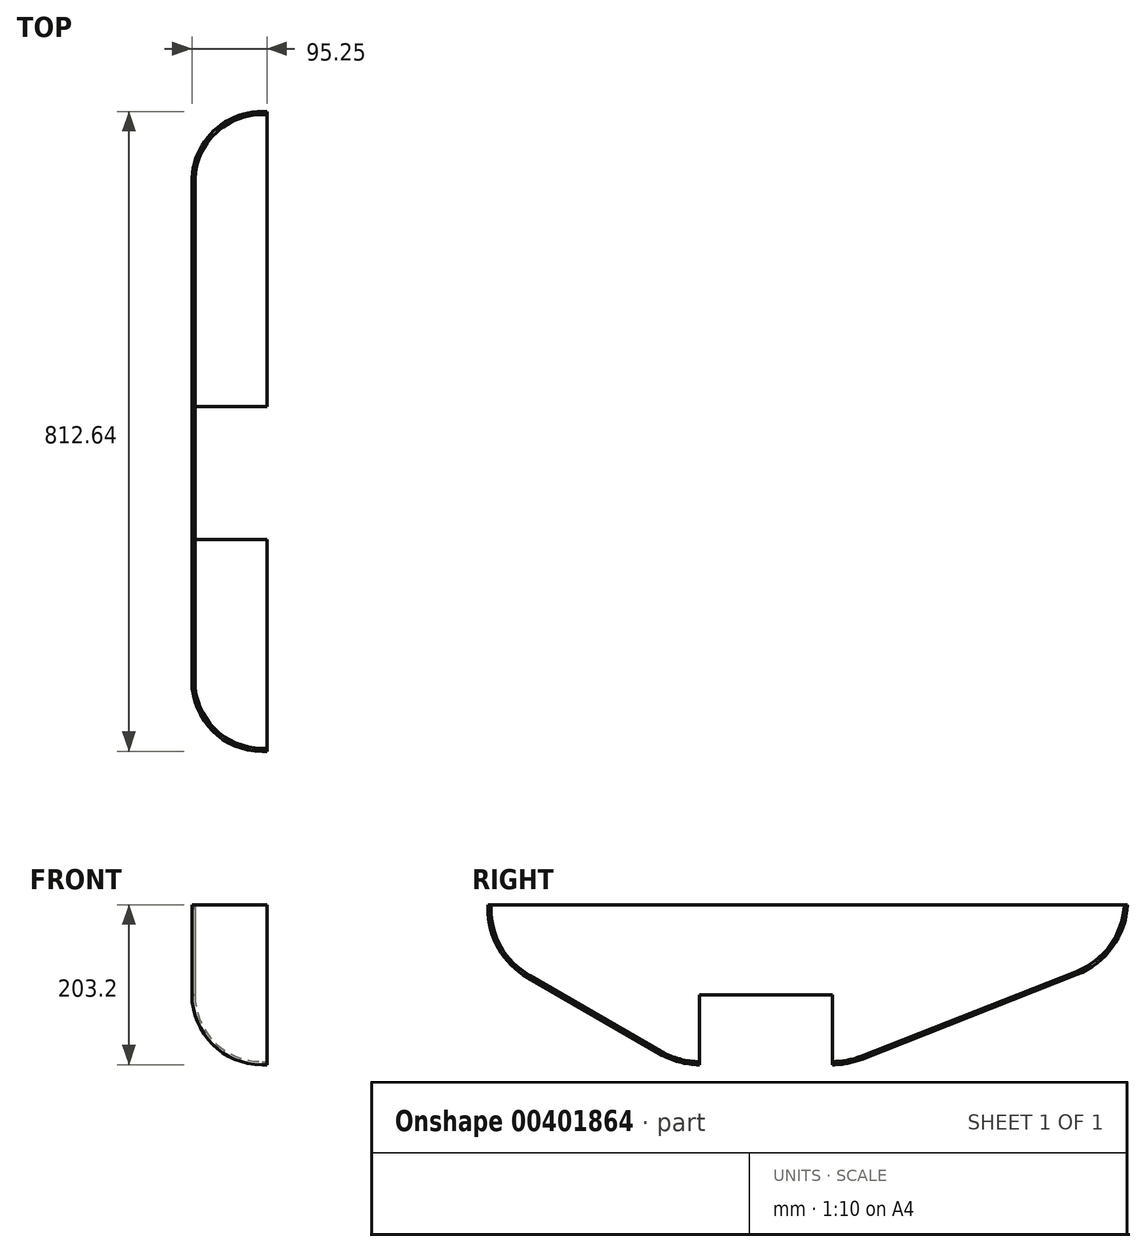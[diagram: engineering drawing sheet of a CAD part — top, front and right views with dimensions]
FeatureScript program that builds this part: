
annotation { "Feature Type Name" : "Feature", "Feature Type Description" : "" }
export const myFeature = defineFeature(function(context is Context, id is Id, definition is map)
    precondition{}
    {
        {
            var Q0;
            Q0=qCreatedBy(makeId("Top.planeOp"),FACE);
            var sketch = newSketch(context, id + "F0", { "sketchPlane" : qUnion([Q0])});
            skLineSegment(sketch, "E0.bottom", {"start": v(95.25, 406.4) * mm, "end": v(-95.25, 406.4) * mm});
            skLineSegment(sketch, "E0.top", {"start": v(95.25, -406.4) * mm, "end": v(-95.25, -406.4) * mm});
            skLineSegment(sketch, "E0.left", {"start": v(95.25, 406.4) * mm, "end": v(95.25, -406.4) * mm});
            skLineSegment(sketch, "E0.right", {"start": v(-95.25, 406.4) * mm, "end": v(-95.25, -406.4) * mm});
            skPoint(sketch, "E0.middle", {"position": v(0, 0) * mm});
            skSolve(sketch);
        }
        {
            var Q0;
            Q0=qSketchRegion(id+"F0",true);
            extrude(context, id + "F1", {"entities" : qUnion([Q0]), "depth" : 406.4 * mm});
        }
        {
            var Q0;
            Q0=makeQuery(id+"F1.opExtrude","CAP_EDGE",EDGE,{"disambiguationData":[OSD([sQuery(id+"F0.wireOp",EDGE,"E0.top")])],"isStart":false});
            var Q1;
            Q1=makeQuery(id+"F1.opExtrude","CAP_EDGE",EDGE,{"disambiguationData":[OSD([sQuery(id+"F0.wireOp",EDGE,"E0.top")])],"isStart":true});
            chamfer(context, id + "F2", {"entities" : qUnion([Q0, Q1]), "chamferType" : ChamferType.OFFSET_ANGLE, "width" : 139.7 * mm, "oppositeDirection" : false, "angle" : 60 * degree, "tangentPropagation" : true});
        }
        {
            var Q0;
            Q0=makeQuery(id+"F1.opExtrude","CAP_EDGE",EDGE,{"disambiguationData":[OSD([sQuery(id+"F0.wireOp",EDGE,"E0.bottom")])],"isStart":false});
            var Q1;
            Q1=makeQuery(id+"F1.opExtrude","CAP_EDGE",EDGE,{"disambiguationData":[OSD([sQuery(id+"F0.wireOp",EDGE,"E0.bottom")])],"isStart":true});
            chamfer(context, id + "F3", {"entities" : qUnion([Q0, Q1]), "chamferType" : ChamferType.TWO_OFFSETS, "width1" : 355.6 * mm, "oppositeDirection" : false, "width2" : 139.7 * mm, "tangentPropagation" : true});
        }
        {
            var Q0;
            {var subQ0=sQuery(id+"F0.wireOp",EDGE,"E0.top");Q0=makeQuery(id+"F2.opChamfer","BLEND_EDGE",EDGE,{"blendedFrom":[makeQuery(id+"F1.opExtrude","CAP_EDGE",EDGE,{"disambiguationData":[OSD([subQ0])],"isStart":false}),makeQuery(id+"F1.opExtrude","SWEPT_FACE",FACE,{"disambiguationData":[OSD([subQ0])]})],"blendedInto":[makeQuery(id+"F1.opExtrude","SWEPT_FACE",FACE,{"disambiguationData":[OSD([subQ0])]})]});}
            var Q1;
            {var subQ0=sQuery(id+"F0.wireOp",EDGE,"E0.top");Q1=makeQuery(id+"F2.opChamfer","BLEND_EDGE",EDGE,{"blendedFrom":[makeQuery(id+"F1.opExtrude","CAP_EDGE",EDGE,{"disambiguationData":[OSD([subQ0])],"isStart":false}),makeQuery(id+"F1.opExtrude","CAP_FACE",FACE,{"disambiguationData":[OSD([sQuery(id+"F0.wireOp",EDGE,"E0.bottom"),subQ0,sQuery(id+"F0.wireOp",EDGE,"E0.left"),sQuery(id+"F0.wireOp",EDGE,"E0.right")])],"isStart":false})],"blendedInto":[makeQuery(id+"F1.opExtrude","CAP_FACE",FACE,{"disambiguationData":[OSD([sQuery(id+"F0.wireOp",EDGE,"E0.bottom"),subQ0,sQuery(id+"F0.wireOp",EDGE,"E0.left"),sQuery(id+"F0.wireOp",EDGE,"E0.right")])],"isStart":false})]});}
            var Q2;
            {var subQ0=sQuery(id+"F0.wireOp",EDGE,"E0.bottom");Q2=makeQuery(id+"F3.opChamfer","BLEND_EDGE",EDGE,{"blendedFrom":[makeQuery(id+"F1.opExtrude","CAP_EDGE",EDGE,{"disambiguationData":[OSD([subQ0])],"isStart":false}),makeQuery(id+"F1.opExtrude","CAP_FACE",FACE,{"disambiguationData":[OSD([subQ0,sQuery(id+"F0.wireOp",EDGE,"E0.top"),sQuery(id+"F0.wireOp",EDGE,"E0.left"),sQuery(id+"F0.wireOp",EDGE,"E0.right")])],"isStart":false})],"blendedInto":[makeQuery(id+"F1.opExtrude","CAP_FACE",FACE,{"disambiguationData":[OSD([subQ0,sQuery(id+"F0.wireOp",EDGE,"E0.top"),sQuery(id+"F0.wireOp",EDGE,"E0.left"),sQuery(id+"F0.wireOp",EDGE,"E0.right")])],"isStart":false})]});}
            var Q3;
            {var subQ0=sQuery(id+"F0.wireOp",EDGE,"E0.bottom");Q3=makeQuery(id+"F3.opChamfer","BLEND_EDGE",EDGE,{"blendedFrom":[makeQuery(id+"F1.opExtrude","CAP_EDGE",EDGE,{"disambiguationData":[OSD([subQ0])],"isStart":false}),makeQuery(id+"F1.opExtrude","SWEPT_FACE",FACE,{"disambiguationData":[OSD([subQ0])]})],"blendedInto":[makeQuery(id+"F1.opExtrude","SWEPT_FACE",FACE,{"disambiguationData":[OSD([subQ0])]})]});}
            var Q4;
            {var subQ0=sQuery(id+"F0.wireOp",EDGE,"E0.bottom");Q4=makeQuery(id+"F3.opChamfer","BLEND_EDGE",EDGE,{"blendedFrom":[makeQuery(id+"F1.opExtrude","CAP_EDGE",EDGE,{"disambiguationData":[OSD([subQ0])],"isStart":true}),makeQuery(id+"F1.opExtrude","SWEPT_FACE",FACE,{"disambiguationData":[OSD([subQ0])]})],"blendedInto":[makeQuery(id+"F1.opExtrude","SWEPT_FACE",FACE,{"disambiguationData":[OSD([subQ0])]})]});}
            var Q5;
            {var subQ0=sQuery(id+"F0.wireOp",EDGE,"E0.bottom");Q5=makeQuery(id+"F3.opChamfer","BLEND_EDGE",EDGE,{"blendedFrom":[makeQuery(id+"F1.opExtrude","CAP_EDGE",EDGE,{"disambiguationData":[OSD([subQ0])],"isStart":true}),makeQuery(id+"F1.opExtrude","CAP_FACE",FACE,{"disambiguationData":[OSD([subQ0,sQuery(id+"F0.wireOp",EDGE,"E0.top"),sQuery(id+"F0.wireOp",EDGE,"E0.left"),sQuery(id+"F0.wireOp",EDGE,"E0.right")])],"isStart":true})],"blendedInto":[makeQuery(id+"F1.opExtrude","CAP_FACE",FACE,{"disambiguationData":[OSD([subQ0,sQuery(id+"F0.wireOp",EDGE,"E0.top"),sQuery(id+"F0.wireOp",EDGE,"E0.left"),sQuery(id+"F0.wireOp",EDGE,"E0.right")])],"isStart":true})]});}
            var Q6;
            {var subQ0=sQuery(id+"F0.wireOp",EDGE,"E0.top");Q6=makeQuery(id+"F2.opChamfer","BLEND_EDGE",EDGE,{"blendedFrom":[makeQuery(id+"F1.opExtrude","CAP_EDGE",EDGE,{"disambiguationData":[OSD([subQ0])],"isStart":true}),makeQuery(id+"F1.opExtrude","CAP_FACE",FACE,{"disambiguationData":[OSD([sQuery(id+"F0.wireOp",EDGE,"E0.bottom"),subQ0,sQuery(id+"F0.wireOp",EDGE,"E0.left"),sQuery(id+"F0.wireOp",EDGE,"E0.right")])],"isStart":true})],"blendedInto":[makeQuery(id+"F1.opExtrude","CAP_FACE",FACE,{"disambiguationData":[OSD([sQuery(id+"F0.wireOp",EDGE,"E0.bottom"),subQ0,sQuery(id+"F0.wireOp",EDGE,"E0.left"),sQuery(id+"F0.wireOp",EDGE,"E0.right")])],"isStart":true})]});}
            var Q7;
            {var subQ0=sQuery(id+"F0.wireOp",EDGE,"E0.top");Q7=makeQuery(id+"F2.opChamfer","BLEND_EDGE",EDGE,{"blendedFrom":[makeQuery(id+"F1.opExtrude","CAP_EDGE",EDGE,{"disambiguationData":[OSD([subQ0])],"isStart":true}),makeQuery(id+"F1.opExtrude","SWEPT_FACE",FACE,{"disambiguationData":[OSD([subQ0])]})],"blendedInto":[makeQuery(id+"F1.opExtrude","SWEPT_FACE",FACE,{"disambiguationData":[OSD([subQ0])]})]});}
            fillet(context, id + "F4", {"entities" : qUnion([Q0, Q1, Q2, Q3, Q4, Q5, Q6, Q7]), "radius" : 101.6 * mm, "tangentPropagation" : true, "allowEdgeOverflow" : false});
        }
        {
            var Q0;
            Q0=makeQuery(id+"F1.opExtrude","SWEPT_FACE",FACE,{"disambiguationData":[OSD([sQuery(id+"F0.wireOp",EDGE,"E0.left")])]});
            var Q1;
            Q1=makeQuery(id+"F1.opExtrude","SWEPT_FACE",FACE,{"disambiguationData":[OSD([sQuery(id+"F0.wireOp",EDGE,"E0.right")])]});
            fillet(context, id + "F5", {"entities" : qUnion([Q0, Q1]), "radius" : 88.9 * mm, "tangentPropagation" : true, "allowEdgeOverflow" : false});
        }
        {
            var Q0;
            {var subQ0=sQuery(id+"F0.wireOp",EDGE,"E0.left");Q0=makeQuery(id+"F5.opFillet","BLEND_FACE",FACE,{"disambiguationData":[OSD([subQ0]),TDD([makeQuery(id+"F1.opExtrude","CAP_EDGE",EDGE,{"disambiguationData":[OSD([subQ0])],"isStart":true})])]});}
            var Q1;
            Q1=makeQuery(id+"F1.opExtrude","CAP_FACE",FACE,{"disambiguationData":[OSD([sQuery(id+"F0.wireOp",EDGE,"E0.bottom"),sQuery(id+"F0.wireOp",EDGE,"E0.top"),sQuery(id+"F0.wireOp",EDGE,"E0.left"),sQuery(id+"F0.wireOp",EDGE,"E0.right")])],"isStart":true});
            var Q2;
            {var subQ0=sQuery(id+"F0.wireOp",EDGE,"E0.right");Q2=makeQuery(id+"F5.opFillet","BLEND_FACE",FACE,{"disambiguationData":[OSD([subQ0]),TDD([makeQuery(id+"F1.opExtrude","CAP_EDGE",EDGE,{"disambiguationData":[OSD([subQ0])],"isStart":true})])]});}
            shell(context, id + "F6", {"entities" : qUnion([Q0, Q1, Q2]), "thickness" : 3.8 * mm});
        }
        {
            var Q0;
            Q0=makeQuery(id+"F1.opExtrude","SWEPT_FACE",FACE,{"disambiguationData":[OSD([sQuery(id+"F0.wireOp",EDGE,"E0.left")])]});
            var sketch = newSketch(context, id + "F7", { "sketchPlane" : qUnion([Q0])});
            skLineSegment(sketch, "E1.bottom", {"start": v(-468.9, 458.17) * mm, "end": v(569.73, 458.17) * mm});
            skLineSegment(sketch, "E1.top", {"start": v(-468.9, 203.2) * mm, "end": v(569.73, 203.2) * mm});
            skLineSegment(sketch, "E1.left", {"start": v(-468.9, 458.17) * mm, "end": v(-468.9, 203.2) * mm});
            skLineSegment(sketch, "E1.right", {"start": v(569.73, 458.17) * mm, "end": v(569.73, 203.2) * mm});
            skFitSpline(sketch, "E2.0", {"points": [v(316.13, 203.2) * mm, v(346.16, 203.2) * mm, v(376.2, 203.2) * mm, v(406.24, 203.2) * mm]});
            skSolve(sketch);
        }
        {
            var Q0;
            Q0 = qSketchRegion(id + "F7", true);
            extrude(context, id + "F8", {"entities" : qUnion([Q0]), "operationType" : NewBodyOperationType.REMOVE, "endBound" : BoundingType.THROUGH_ALL, "oppositeDirection" : true, "depth" : 25.4 * mm});
        }
        {
            var Q0;
            {var subQ0=sQuery(id+"F7.wireOp",EDGE,"E1.top");var subQ1=sQuery(id+"F0.wireOp",EDGE,"E0.left");var subQ2=makeQuery(id+"F1.opExtrude","SWEPT_FACE",FACE,{"disambiguationData":[OSD([subQ1])]});var subQ3=subQ2;var subQ6=makeQuery(id+"F7.imprint","INTERSECT",VERTEX,{"derivedFrom":[makeQuery(id+"F5.opFillet","BLEND_EDGE",EDGE,{"blendedFrom":[makeQuery(id+"F1.opExtrude","SWEPT_EDGE",EDGE,{"disambiguationData":[OSD([sQuery(id+"F0.wireOp",EDGE,"E0.top"),subQ1])]}),subQ3],"blendedInto":[subQ3]}),subQ0]});Q0=makeQuery(id+"F8.boolean.opBoolean","COPY",FACE,{"derivedFrom":makeQuery(id+"F8.opExtrude","SWEPT_FACE",FACE,{"disambiguationData":[OSD([subQ0]),TDD([makeQuery(id+"F7.imprint","IMPRINT",EDGE,{"disambiguationData":[TD([[makeQuery(id+"F7.imprint","INTERSECT",VERTEX,{"derivedFrom":[subQ0,sQuery(id+"F7.wireOp",EDGE,"E1.left")]}),-1.0]])],"derivedFrom":subQ0}),makeQuery(id+"F7.imprint","IMPRINT",EDGE,{"disambiguationData":[TD([[subQ6,-1.0]])],"derivedFrom":subQ0})])]})});}
            var sketch = newSketch(context, id + "F9", { "sketchPlane" : qUnion([Q0])});
            skLineSegment(sketch, "E3.bottom", {"start": v(0, 592.36) * mm, "end": v(292.27, 592.36) * mm});
            skLineSegment(sketch, "E3.top", {"start": v(0, -554.6) * mm, "end": v(292.27, -554.6) * mm});
            skLineSegment(sketch, "E3.left", {"start": v(0, 592.36) * mm, "end": v(0, -554.6) * mm});
            skLineSegment(sketch, "E3.right", {"start": v(292.27, 592.36) * mm, "end": v(292.27, -554.6) * mm});
            skSolve(sketch);
        }
        {
            var Q0;
            Q0 = qSketchRegion(id + "F9", true);
            extrude(context, id + "F10", {"entities" : qUnion([Q0]), "operationType" : NewBodyOperationType.REMOVE, "endBound" : BoundingType.THROUGH_ALL, "oppositeDirection" : true, "depth" : 25.4 * mm});
        }
    });
